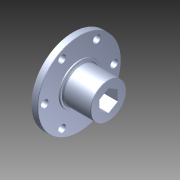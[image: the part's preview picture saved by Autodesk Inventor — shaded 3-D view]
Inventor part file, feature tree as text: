
AUTODESK INVENTOR PART (.ipt)
format: ipt  version: 2015 SP1 (Build 190203100, 203)  size: 163,328 bytes
history: native  units: in
note: dims shown in document units (in); Inventor stores cm internally (conversion verified against a paired STEP export)
features: chamfer x1, other x1, imported_body x1
ambient origin geometry x8: Origin, YZ Plane, XZ Plane, XY Plane, X Axis, Y Axis, Z Axis, Center Point
bodies: Body1 (feature_tree)
feature tree (3):
  chamfer  "Chamfer3"  [1 undecoded]
  other  "hub hex 0.5in1"
  imported_body  "Base1"
note: 1 required parameter value undecoded (feature->parameter linkage not recoverable at this tier; creation-order binding heuristic only, values carry confidence <= 0.55)
